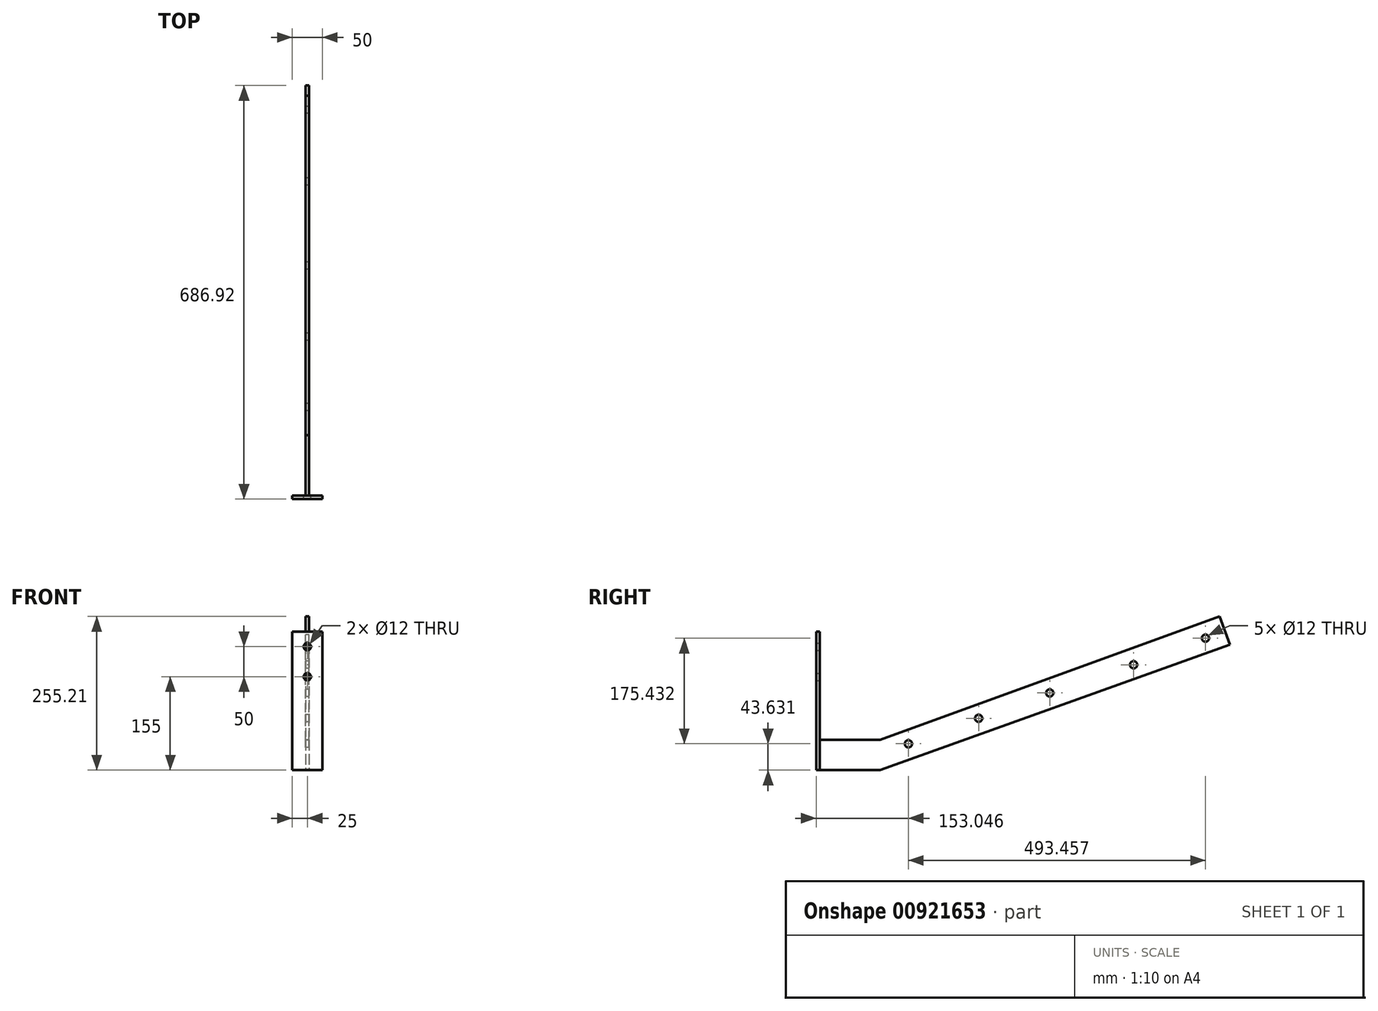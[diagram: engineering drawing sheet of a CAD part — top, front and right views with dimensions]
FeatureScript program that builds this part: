
annotation { "Feature Type Name" : "Feature", "Feature Type Description" : "" }
export const myFeature = defineFeature(function(context is Context, id is Id, definition is map)
    precondition{}
    {
        {
            var Q0;
            Q0=qCreatedBy(makeId("Right.planeOp"),FACE);
            var sketch = newSketch(context, id + "F0", { "sketchPlane" : qUnion([Q0])});
            skLineSegment(sketch, "E0", {"start": v(6, 50) * mm, "end": v(106, 50) * mm});
            skLineSegment(sketch, "E1", {"start": v(106, 50) * mm, "end": v(669.82, 255.21) * mm});
            skLineSegment(sketch, "E2", {"start": v(669.82, 255.21) * mm, "end": v(686.92, 208.23) * mm});
            skLineSegment(sketch, "E3", {"start": v(686.92, 208.23) * mm, "end": v(106, 0) * mm});
            skLineSegment(sketch, "E4", {"start": v(106, 0) * mm, "end": v(6, 0) * mm});
            skLineSegment(sketch, "E5", {"start": v(6, 50) * mm, "end": v(6, 0) * mm});
            skPoint(sketch, "E6.orphan", {"position": v(0, 0) * mm});
            skCircle(sketch, "E7", {"center": v(387.9, 128.05) * mm, "radius": 6 * mm});
            skPoint(sketch, "E7.centerSnap0", {"position": v(387.9, 152.6) * mm});
            skCircle(sketch, "E8", {"center": v(527.24, 174.99) * mm, "radius": 6 * mm});
            skCircle(sketch, "E9", {"center": v(646.5, 219.06) * mm, "radius": 6 * mm});
            skCircle(sketch, "E10", {"center": v(269.71, 85.98) * mm, "radius": 6 * mm});
            skCircle(sketch, "E11", {"center": v(153.05, 43.63) * mm, "radius": 6 * mm});
            skSolve(sketch);
        }
        {
            var Q0;
            Q0 = qSketchRegion(id + "F0", true);
            extrude(context, id + "F1", {"entities" : qUnion([Q0]), "depth" : 6 * mm, "offsetDistance" : 25 * mm});
        }
        {
            var Q0;
            Q0=makeQuery(id+"F1.opExtrude","SWEPT_FACE",FACE,{"disambiguationData":[OSD([sQuery(id+"F0.wireOp",EDGE,"E5")])]});
            var sketch = newSketch(context, id + "F2", { "sketchPlane" : qUnion([Q0])});
            skLineSegment(sketch, "E12", {"start": v(6, 0) * mm, "end": v(28, 0) * mm});
            skLineSegment(sketch, "E13", {"start": v(28, 0) * mm, "end": v(28, 230) * mm});
            skLineSegment(sketch, "E14", {"start": v(28, 230) * mm, "end": v(-22, 230) * mm});
            skLineSegment(sketch, "E15", {"start": v(-22, 230) * mm, "end": v(-22, 0) * mm});
            skLineSegment(sketch, "E16", {"start": v(-22, 0) * mm, "end": v(6, 0) * mm});
            skCircle(sketch, "E17", {"center": v(3, 205) * mm, "radius": 6 * mm});
            skPoint(sketch, "E17.centerSnap0", {"position": v(3, 230) * mm});
            skCircle(sketch, "E18", {"center": v(3, 155) * mm, "radius": 6 * mm});
            skSolve(sketch);
        }
        {
            var Q0;
            Q0 = qSketchRegion(id + "F2", true);
            extrude(context, id + "F3", {"entities" : qUnion([Q0]), "operationType" : NewBodyOperationType.ADD, "depth" : 6 * mm, "offsetDistance" : 25 * mm});
        }
    });
